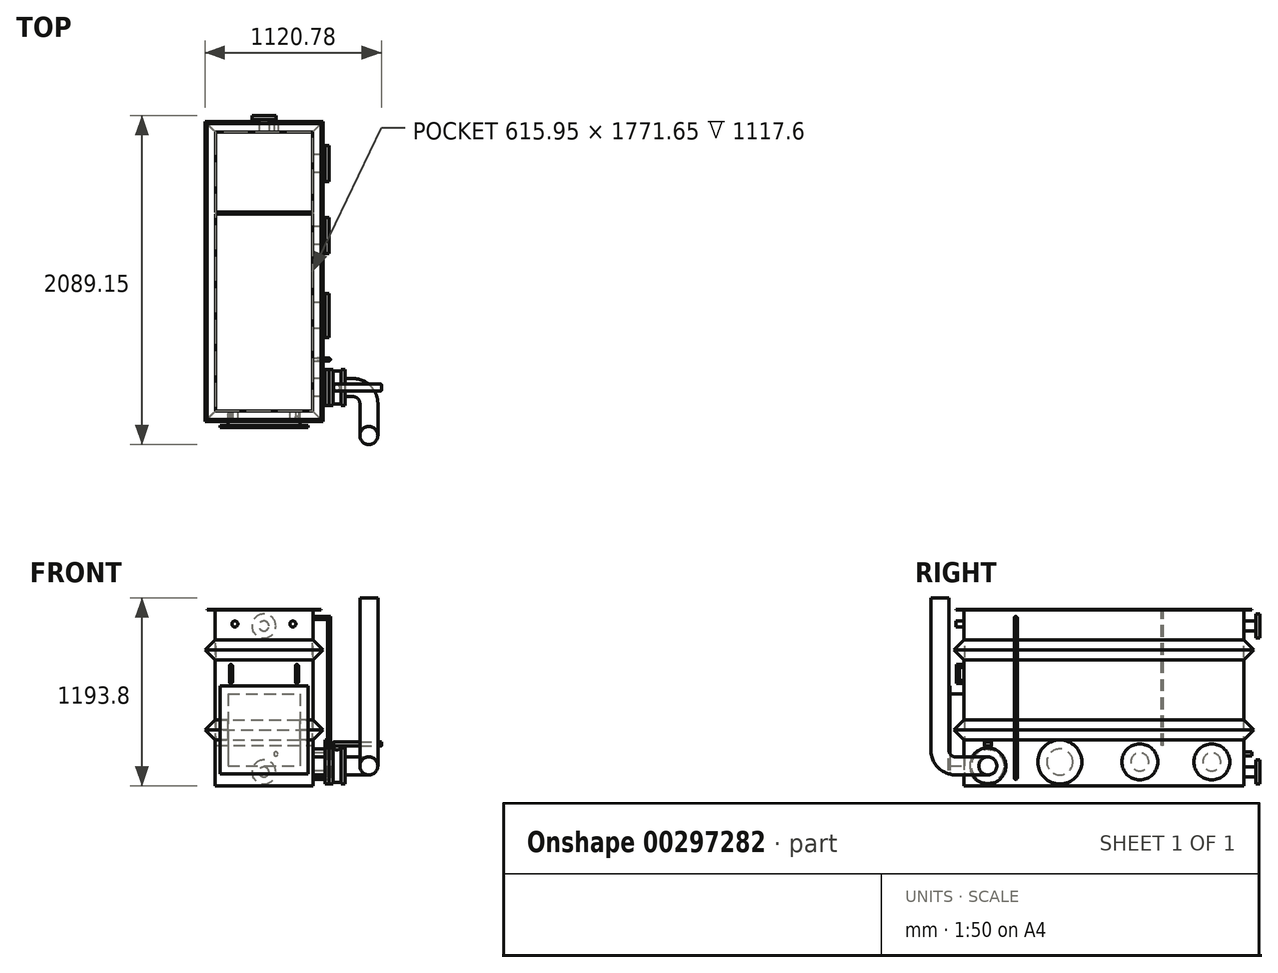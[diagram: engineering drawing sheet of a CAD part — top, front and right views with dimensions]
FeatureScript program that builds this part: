
annotation { "Feature Type Name" : "Feature", "Feature Type Description" : "" }
export const myFeature = defineFeature(function(context is Context, id is Id, definition is map)
    precondition{}
    {
        {
            var Q0;
            Q0=qCreatedBy(makeId("Top.planeOp"),FACE);
            var sketch = newSketch(context, id + "F0", { "sketchPlane" : qUnion([Q0])});
            skLineSegment(sketch, "E0.bottom", {"start": v(-311.15, 889) * mm, "end": v(311.15, 889) * mm});
            skLineSegment(sketch, "E0.top", {"start": v(-311.15, -889) * mm, "end": v(311.15, -889) * mm});
            skLineSegment(sketch, "E0.left", {"start": v(-311.15, 889) * mm, "end": v(-311.15, -889) * mm});
            skLineSegment(sketch, "E0.right", {"start": v(311.15, 889) * mm, "end": v(311.15, -889) * mm});
            skPoint(sketch, "E0.middle", {"position": v(0, 0) * mm});
            skSolve(sketch);
        }
        {
            var Q0;
            Q0 = qSketchRegion(id + "F0", true);
            extrude(context, id + "F1", {"entities" : qUnion([Q0]), "depth" : 558.8 * mm, "hasSecondDirection" : true, "secondDirectionOppositeDirection" : true, "secondDirectionDepth" : 558.8 * mm});
        }
        {
            var Q0;
            Q0=makeQuery(id+"F1.opExtrude","CAP_FACE",FACE,{"disambiguationData":[OSD([sQuery(id+"F0.wireOp",EDGE,"E0.bottom"),sQuery(id+"F0.wireOp",EDGE,"E0.top"),sQuery(id+"F0.wireOp",EDGE,"E0.left"),sQuery(id+"F0.wireOp",EDGE,"E0.right")])],"isStart":false});
            shell(context, id + "F2", {"entities" : qUnion([Q0]), "thickness" : 3.17 * mm});
        }
        {
            var Q0;
            Q0=makeQuery(id+"F1.opExtrude","CAP_FACE",FACE,{"disambiguationData":[OSD([sQuery(id+"F0.wireOp",EDGE,"E0.bottom"),sQuery(id+"F0.wireOp",EDGE,"E0.top"),sQuery(id+"F0.wireOp",EDGE,"E0.left"),sQuery(id+"F0.wireOp",EDGE,"E0.right")])],"isStart":false});
            var sketch = newSketch(context, id + "F3", { "sketchPlane" : qUnion([Q0])});
            skLineSegment(sketch, "E1.bottom", {"start": v(-361.95, 939.8) * mm, "end": v(361.95, 939.8) * mm});
            skLineSegment(sketch, "E1.top", {"start": v(-361.95, -939.8) * mm, "end": v(361.95, -939.8) * mm});
            skLineSegment(sketch, "E1.left", {"start": v(-361.95, 939.8) * mm, "end": v(-361.95, -939.8) * mm});
            skLineSegment(sketch, "E1.right", {"start": v(361.95, 939.8) * mm, "end": v(361.95, -939.8) * mm});
            skLineSegment(sketch, "E2.bottom", {"start": v(-307.97, 885.83) * mm, "end": v(307.97, 885.83) * mm});
            skLineSegment(sketch, "E2.top", {"start": v(-307.97, -885.83) * mm, "end": v(307.97, -885.83) * mm});
            skLineSegment(sketch, "E2.left", {"start": v(-307.97, 885.83) * mm, "end": v(-307.97, -885.83) * mm});
            skLineSegment(sketch, "E2.right", {"start": v(307.97, 885.83) * mm, "end": v(307.97, -885.83) * mm});
            skSolve(sketch);
        }
        {
            var Q0;
            Q0 = qSketchRegion(id + "F3", true);
            extrude(context, id + "F4", {"entities" : qUnion([Q0]), "operationType" : NewBodyOperationType.ADD, "depth" : 3.17 * mm});
        }
        {
            var Q0;
            Q0=makeQuery(id+"F1.opExtrude","SWEPT_FACE",FACE,{"disambiguationData":[OSD([sQuery(id+"F0.wireOp",EDGE,"E0.right")])]});
            var sketch = newSketch(context, id + "F5", { "sketchPlane" : qUnion([Q0])});
            skLineSegment(sketch, "E3", {"start": v(-889, 368.3) * mm, "end": v(-952.5, 304.8) * mm});
            skLineSegment(sketch, "E4", {"start": v(-952.5, 304.8) * mm, "end": v(-889, 241.3) * mm});
            skLineSegment(sketch, "E5", {"start": v(-889, 241.3) * mm, "end": v(-889, 368.3) * mm});
            skLineSegment(sketch, "E6", {"start": v(-889, -139.7) * mm, "end": v(-952.5, -203.2) * mm});
            skLineSegment(sketch, "E7", {"start": v(-952.5, -203.2) * mm, "end": v(-889, -266.7) * mm});
            skLineSegment(sketch, "E8", {"start": v(-889, -266.7) * mm, "end": v(-889, -139.7) * mm});
            skSolve(sketch);
        }
        {
            var Q0;
            Q0 = qSketchRegion(id + "F5", true);
            var Q1;
            Q1=makeQuery(id+"F1.opExtrude","CAP_EDGE",EDGE,{"disambiguationData":[OSD([sQuery(id+"F0.wireOp",EDGE,"E0.top")])],"isStart":true});
            var Q2;
            Q2=makeQuery(id+"F1.opExtrude","CAP_EDGE",EDGE,{"disambiguationData":[OSD([sQuery(id+"F0.wireOp",EDGE,"E0.left")])],"isStart":true});
            var Q3;
            Q3=makeQuery(id+"F1.opExtrude","CAP_EDGE",EDGE,{"disambiguationData":[OSD([sQuery(id+"F0.wireOp",EDGE,"E0.bottom")])],"isStart":true});
            var Q4;
            Q4=makeQuery(id+"F1.opExtrude","CAP_EDGE",EDGE,{"disambiguationData":[OSD([sQuery(id+"F0.wireOp",EDGE,"E0.right")])],"isStart":true});
            sweep(context, id + "F6", {"operationType" : NewBodyOperationType.ADD, "profiles" : qUnion([Q0]), "path" : qUnion([Q1, Q2, Q3, Q4])});
        }
        {
            var Q0;
            {var subQ1=sQuery(id+"F0.wireOp",EDGE,"E0.top");var subQ4=sQuery(id+"F5.wireOp",EDGE,"E4");Q0=makeQuery(id+"F6.boolean.opBoolean","SPLIT",FACE,{"disambiguationData":[TD([makeQuery(id+"F6.opSweep","SWEPT_FACE",FACE,{"disambiguationData":[OSD([subQ1,subQ4])]})])],"derivedFrom":makeQuery(id+"F1.opExtrude","SWEPT_FACE",FACE,{"disambiguationData":[OSD([subQ1])]})});}
            var sketch = newSketch(context, id + "F7", { "sketchPlane" : qUnion([Q0])});
            skLineSegment(sketch, "E9.bottom", {"start": v(-228.6, 25.4) * mm, "end": v(228.6, 25.4) * mm});
            skLineSegment(sketch, "E9.top", {"start": v(-228.6, -431.8) * mm, "end": v(228.6, -431.8) * mm});
            skLineSegment(sketch, "E9.left", {"start": v(-228.6, 25.4) * mm, "end": v(-228.6, -431.8) * mm});
            skLineSegment(sketch, "E9.right", {"start": v(228.6, 25.4) * mm, "end": v(228.6, -431.8) * mm});
            skSolve(sketch);
        }
        {
            var Q0;
            Q0 = qSketchRegion(id + "F7", true);
            extrude(context, id + "F8", {"entities" : qUnion([Q0]), "operationType" : NewBodyOperationType.ADD, "depth" : 88.9 * mm});
        }
        {
            var Q0;
            Q0=makeQuery(id+"F8.opExtrude","CAP_FACE",FACE,{"disambiguationData":[OSD([sQuery(id+"F7.wireOp",EDGE,"E9.bottom"),sQuery(id+"F7.wireOp",EDGE,"E9.top"),sQuery(id+"F7.wireOp",EDGE,"E9.left"),sQuery(id+"F7.wireOp",EDGE,"E9.right")])],"isStart":false});
            var sketch = newSketch(context, id + "F9", { "sketchPlane" : qUnion([Q0])});
            skLineSegment(sketch, "E10.bottom", {"start": v(-279.4, 76.2) * mm, "end": v(279.4, 76.2) * mm});
            skLineSegment(sketch, "E10.top", {"start": v(-279.4, -482.6) * mm, "end": v(279.4, -482.6) * mm});
            skLineSegment(sketch, "E10.left", {"start": v(-279.4, 76.2) * mm, "end": v(-279.4, -482.6) * mm});
            skLineSegment(sketch, "E10.right", {"start": v(279.4, 76.2) * mm, "end": v(279.4, -482.6) * mm});
            skPoint(sketch, "E10.middle", {"position": v(0, -203.2) * mm});
            skSolve(sketch);
        }
        {
            var Q0;
            Q0=makeQuery(id+"F9.imprint","IMPRINT",FACE,{"disambiguationData":[TD([[makeQuery(id+"F9.imprint","IMPRINT",EDGE,{"derivedFrom":sQuery(id+"F9.wireOp",EDGE,"E10.bottom")}),-1.0]])]});
            var Q1;
            Q1=makeQuery(id+"F9.imprint","IMPRINT",FACE,{"disambiguationData":[TD([[makeQuery(id+"F9.imprint","IMPRINT",EDGE,{"derivedFrom":makeQuery(id+"F8.opExtrude","CAP_EDGE",EDGE,{"disambiguationData":[OSD([sQuery(id+"F7.wireOp",EDGE,"E9.bottom")])],"isStart":false})}),-1.0]])]});
            extrude(context, id + "F10", {"entities" : qUnion([Q0, Q1]), "operationType" : NewBodyOperationType.ADD, "depth" : 12.7 * mm});
        }
        {
            var Q0;
            {var subQ0=sQuery(id+"F5.wireOp",EDGE,"E4");var subQ1=sQuery(id+"F0.wireOp",EDGE,"E0.bottom");var subQ3=sQuery(id+"F0.wireOp",EDGE,"E0.right");Q0=makeQuery(id+"F6.boolean.opBoolean","SPLIT",FACE,{"disambiguationData":[TD([makeQuery(id+"F6.opSweep","SWEPT_FACE",FACE,{"disambiguationData":[OSD([subQ1,subQ0])]})])],"derivedFrom":makeQuery(id+"F1.opExtrude","SWEPT_FACE",FACE,{"disambiguationData":[OSD([subQ3])]})});}
            var sketch = newSketch(context, id + "F11", { "sketchPlane" : qUnion([Q0])});
            skCircle(sketch, "E11", {"center": v(-279.4, -406.4) * mm, "radius": 82.55 * mm});
            skCircle(sketch, "E12", {"center": v(228.6, -406.4) * mm, "radius": 57.15 * mm});
            skCircle(sketch, "E13", {"center": v(685.8, -406.4) * mm, "radius": 57.15 * mm});
            skSolve(sketch);
        }
        {
            var Q0;
            Q0 = qSketchRegion(id + "F11", true);
            extrude(context, id + "F12", {"entities" : qUnion([Q0]), "operationType" : NewBodyOperationType.ADD, "depth" : 76.2 * mm});
        }
        {
            var Q0;
            Q0=makeQuery(id+"F12.opExtrude","CAP_FACE",FACE,{"disambiguationData":[OSD([sQuery(id+"F11.wireOp",EDGE,"E13")])],"isStart":false});
            var sketch = newSketch(context, id + "F13", { "sketchPlane" : qUnion([Q0])});
            skCircle(sketch, "E14", {"center": v(-279.4, -406.4) * mm, "radius": 139.7 * mm});
            skCircle(sketch, "E15", {"center": v(228.6, -406.4) * mm, "radius": 114.3 * mm});
            skCircle(sketch, "E16", {"center": v(685.8, -406.4) * mm, "radius": 114.3 * mm});
            skSolve(sketch);
        }
        {
            var Q0;
            Q0 = qSketchRegion(id + "F13", true);
            extrude(context, id + "F14", {"entities" : qUnion([Q0]), "operationType" : NewBodyOperationType.ADD, "depth" : 25.4 * mm});
        }
        {
            var Q0;
            {var subQ0=sQuery(id+"F5.wireOp",EDGE,"E4");var subQ1=sQuery(id+"F0.wireOp",EDGE,"E0.bottom");var subQ3=sQuery(id+"F0.wireOp",EDGE,"E0.right");Q0=makeQuery(id+"F6.boolean.opBoolean","SPLIT",FACE,{"disambiguationData":[TD([makeQuery(id+"F6.opSweep","SWEPT_FACE",FACE,{"disambiguationData":[OSD([subQ1,subQ0])]})])],"derivedFrom":makeQuery(id+"F1.opExtrude","SWEPT_FACE",FACE,{"disambiguationData":[OSD([subQ3])]})});}
            var sketch = newSketch(context, id + "F15", { "sketchPlane" : qUnion([Q0])});
            skCircle(sketch, "E17", {"center": v(-558.8, 508) * mm, "radius": 9.53 * mm});
            skCircle(sketch, "E18", {"center": v(-558.8, -508) * mm, "radius": 9.53 * mm});
            skSolve(sketch);
        }
        {
            var Q0;
            {var subQ0=sQuery(id+"F5.wireOp",EDGE,"E3");var subQ1=sQuery(id+"F0.wireOp",EDGE,"E0.top");Q0=makeQuery(id+"F6.boolean.opBoolean","SPLIT",FACE,{"disambiguationData":[TD([makeQuery(id+"F6.opSweep","SWEPT_FACE",FACE,{"disambiguationData":[OSD([subQ1,subQ0])]})])],"derivedFrom":makeQuery(id+"F1.opExtrude","SWEPT_FACE",FACE,{"disambiguationData":[OSD([subQ1])]})});}
            var sketch = newSketch(context, id + "F16", { "sketchPlane" : qUnion([Q0])});
            skLineSegment(sketch, "E19", {"start": v(311.15, 508) * mm, "end": v(412.75, 508) * mm});
            skLineSegment(sketch, "E20", {"start": v(412.75, 508) * mm, "end": v(412.75, -508) * mm});
            skLineSegment(sketch, "E21", {"start": v(412.75, -508) * mm, "end": v(311.15, -508) * mm});
            skSolve(sketch);
        }
        {
            var Q0;
            Q0=makeQuery(id+"F15.imprint","IMPRINT",FACE,{"disambiguationData":[TD([[makeQuery(id+"F15.imprint","IMPRINT",EDGE,{"derivedFrom":sQuery(id+"F15.wireOp",EDGE,"E17")}),1.0]])]});
            var Q1;
            Q1=sQuery(id+"F16.wireOp",EDGE,"E19");
            var Q2;
            Q2=sQuery(id+"F16.wireOp",EDGE,"E20");
            var Q3;
            Q3=sQuery(id+"F16.wireOp",EDGE,"E21");
            sweep(context, id + "F17", {"operationType" : NewBodyOperationType.ADD, "profiles" : qUnion([Q0]), "path" : qUnion([Q1, Q2, Q3])});
        }
        {
            var Q0;
            Q0=makeQuery(id+"F4.opExtrude","CAP_FACE",FACE,{"disambiguationData":[OSD([sQuery(id+"F3.wireOp",EDGE,"E1.bottom"),sQuery(id+"F3.wireOp",EDGE,"E1.top"),sQuery(id+"F3.wireOp",EDGE,"E1.left"),sQuery(id+"F3.wireOp",EDGE,"E1.right"),sQuery(id+"F3.wireOp",EDGE,"E2.bottom"),sQuery(id+"F3.wireOp",EDGE,"E2.top"),sQuery(id+"F3.wireOp",EDGE,"E2.left"),sQuery(id+"F3.wireOp",EDGE,"E2.right")])],"isStart":false});
            var sketch = newSketch(context, id + "F18", { "sketchPlane" : qUnion([Q0])});
            skLineSegment(sketch, "E22.bottom", {"start": v(-307.98, 377.83) * mm, "end": v(307.98, 377.83) * mm});
            skLineSegment(sketch, "E22.top", {"start": v(-307.98, 365.13) * mm, "end": v(307.98, 365.13) * mm});
            skLineSegment(sketch, "E22.left", {"start": v(-307.98, 377.83) * mm, "end": v(-307.98, 365.13) * mm});
            skLineSegment(sketch, "E22.right", {"start": v(307.98, 377.83) * mm, "end": v(307.98, 365.13) * mm});
            skSolve(sketch);
        }
        {
            var Q0;
            Q0 = qSketchRegion(id + "F18", true);
            extrude(context, id + "F19", {"entities" : qUnion([Q0]), "operationType" : NewBodyOperationType.ADD, "oppositeDirection" : true, "depth" : 863.6 * mm});
        }
        {
            var Q0;
            {var subQ0=sQuery(id+"F5.wireOp",EDGE,"E4");var subQ1=sQuery(id+"F0.wireOp",EDGE,"E0.bottom");Q0=makeQuery(id+"F6.boolean.opBoolean","SPLIT",FACE,{"disambiguationData":[TD([makeQuery(id+"F6.opSweep","SWEPT_FACE",FACE,{"disambiguationData":[OSD([subQ1,subQ0])]})])],"derivedFrom":makeQuery(id+"F1.opExtrude","SWEPT_FACE",FACE,{"disambiguationData":[OSD([subQ1])]})});}
            var sketch = newSketch(context, id + "F20", { "sketchPlane" : qUnion([Q0])});
            skCircle(sketch, "E23", {"center": v(0, 457.2) * mm, "radius": 31.75 * mm});
            skCircle(sketch, "E24", {"center": v(0, -469.9) * mm, "radius": 31.75 * mm});
            skSolve(sketch);
        }
        {
            var Q0;
            Q0 = qSketchRegion(id + "F20", true);
            extrude(context, id + "F21", {"entities" : qUnion([Q0]), "operationType" : NewBodyOperationType.ADD, "depth" : 76.2 * mm});
        }
        {
            var Q0;
            {var subQ2=sQuery(id+"F5.wireOp",EDGE,"E7");var subQ3=sQuery(id+"F0.wireOp",EDGE,"E0.bottom");Q0=makeQuery(id+"F6.boolean.opBoolean","SPLIT",FACE,{"disambiguationData":[TD([makeQuery(id+"F6.opSweep","SWEPT_FACE",FACE,{"disambiguationData":[OSD([subQ3,subQ2])]})])],"derivedFrom":makeQuery(id+"F1.opExtrude","SWEPT_FACE",FACE,{"disambiguationData":[OSD([subQ3])]})});}
            var sketch = newSketch(context, id + "F22", { "sketchPlane" : qUnion([Q0])});
            skCircle(sketch, "E25", {"center": v(-76.2, -355.6) * mm, "radius": 12.7 * mm});
            skSolve(sketch);
        }
        {
            var Q0;
            Q0 = qSketchRegion(id + "F22", true);
            extrude(context, id + "F23", {"entities" : qUnion([Q0]), "operationType" : NewBodyOperationType.ADD, "depth" : 50.8 * mm});
        }
        {
            var Q0;
            {var subQ1=sQuery(id+"F5.wireOp",EDGE,"E7");var subQ2=sQuery(id+"F0.wireOp",EDGE,"E0.bottom");var subQ3=sQuery(id+"F0.wireOp",EDGE,"E0.right");Q0=makeQuery(id+"F6.boolean.opBoolean","SPLIT",FACE,{"disambiguationData":[TD([makeQuery(id+"F6.opSweep","SWEPT_FACE",FACE,{"disambiguationData":[OSD([subQ2,subQ1])]})])],"derivedFrom":makeQuery(id+"F1.opExtrude","SWEPT_FACE",FACE,{"disambiguationData":[OSD([subQ3])]})});}
            var sketch = newSketch(context, id + "F24", { "sketchPlane" : qUnion([Q0])});
            skCircle(sketch, "E26", {"center": v(-736.6, -431.8) * mm, "radius": 57.15 * mm});
            skSolve(sketch);
        }
        {
            var Q0;
            Q0=makeQuery(id+"F24.imprint","IMPRINT",FACE,{"disambiguationData":[TD([[makeQuery(id+"F24.imprint","IMPRINT",EDGE,{"derivedFrom":sQuery(id+"F24.wireOp",EDGE,"E26")}),1.0]])]});
            extrude(context, id + "F25", {"entities" : qUnion([Q0]), "operationType" : NewBodyOperationType.ADD, "depth" : 76.2 * mm});
        }
        {
            var Q0;
            Q0=makeQuery(id+"F25.opExtrude","CAP_FACE",FACE,{"disambiguationData":[OSD([sQuery(id+"F24.wireOp",EDGE,"E26")])],"isStart":false});
            var sketch = newSketch(context, id + "F26", { "sketchPlane" : qUnion([Q0])});
            skCircle(sketch, "E27", {"center": v(-736.6, -431.8) * mm, "radius": 114.3 * mm});
            skSolve(sketch);
        }
        {
            var Q0;
            Q0 = qSketchRegion(id + "F26", true);
            extrude(context, id + "F27", {"entities" : qUnion([Q0]), "operationType" : NewBodyOperationType.ADD, "depth" : 25.4 * mm});
        }
        {
            var Q0;
            Q0=makeQuery(id+"F27.opExtrude","CAP_FACE",FACE,{"disambiguationData":[OSD([sQuery(id+"F26.wireOp",EDGE,"E27")])],"isStart":false});
            var sketch = newSketch(context, id + "F28", { "sketchPlane" : qUnion([Q0])});
            skCircle(sketch, "E28", {"center": v(-736.6, -431.8) * mm, "radius": 114.3 * mm});
            skSolve(sketch);
        }
        {
            var Q0;
            Q0=makeQuery(id+"F28.imprint","IMPRINT",FACE,{"disambiguationData":[TD([[makeQuery(id+"F28.imprint","IMPRINT",EDGE,{"derivedFrom":sQuery(id+"F28.wireOp",EDGE,"E28")}),1.0]])]});
            extrude(context, id + "F29", {"entities" : qUnion([Q0]), "depth" : 25.4 * mm});
        }
        {
            var Q0;
            Q0=makeQuery(id+"F29.opExtrude","CAP_FACE",FACE,{"disambiguationData":[OSD([sQuery(id+"F28.wireOp",EDGE,"E28")])],"isStart":false});
            var sketch = newSketch(context, id + "F30", { "sketchPlane" : qUnion([Q0])});
            skCircle(sketch, "E29", {"center": v(-736.6, -431.8) * mm, "radius": 104.78 * mm});
            skSolve(sketch);
        }
        {
            var Q0;
            Q0 = qSketchRegion(id + "F30", true);
            extrude(context, id + "F31", {"entities" : qUnion([Q0]), "depth" : 50.8 * mm});
        }
        {
            var Q0;
            Q0=makeQuery(id+"F31.opExtrude","CAP_FACE",FACE,{"disambiguationData":[OSD([sQuery(id+"F30.wireOp",EDGE,"E29")])],"isStart":false});
            var sketch = newSketch(context, id + "F32", { "sketchPlane" : qUnion([Q0])});
            skCircle(sketch, "E30", {"center": v(-736.6, -431.8) * mm, "radius": 114.3 * mm});
            skSolve(sketch);
        }
        {
            var Q0;
            Q0 = qSketchRegion(id + "F32", true);
            extrude(context, id + "F33", {"entities" : qUnion([Q0]), "depth" : 25.4 * mm});
        }
        {
            var Q0;
            Q0=makeQuery(id+"F33.opExtrude","CAP_FACE",FACE,{"disambiguationData":[OSD([sQuery(id+"F32.wireOp",EDGE,"E30")])],"isStart":false});
            var sketch = newSketch(context, id + "F34", { "sketchPlane" : qUnion([Q0])});
            skCircle(sketch, "E31", {"center": v(-736.6, -431.8) * mm, "radius": 57.15 * mm});
            skSolve(sketch);
        }
        {
            var Q0;
            Q0=makeQuery(id+"F1.opExtrude","CAP_FACE",FACE,{"disambiguationData":[OSD([sQuery(id+"F0.wireOp",EDGE,"E0.bottom"),sQuery(id+"F0.wireOp",EDGE,"E0.top"),sQuery(id+"F0.wireOp",EDGE,"E0.left"),sQuery(id+"F0.wireOp",EDGE,"E0.right")])],"isStart":true});
            var sketch = newSketch(context, id + "F35", { "sketchPlane" : qUnion([Q0])});
            skLineSegment(sketch, "E32", {"start": v(514.35, 736.6) * mm, "end": v(565.15, 736.6) * mm});
            skLineSegment(sketch, "E33", {"start": v(666.75, 838.2) * mm, "end": v(666.75, 889) * mm});
            skPoint(sketch, "E34.visualSharp", {"position": v(666.75, 736.6) * mm});
            skArc(sketch, "E34.filletArc", {"start": v(565.15, 736.6) * mm, "mid": v(637, 766.36) * mm, "end": v(666.75, 838.2) * mm});
            skSolve(sketch);
        }
        {
            var Q0;
            Q0=makeQuery(id+"F34.imprint","IMPRINT",FACE,{"disambiguationData":[TD([[makeQuery(id+"F34.imprint","IMPRINT",EDGE,{"derivedFrom":sQuery(id+"F34.wireOp",EDGE,"E31")}),1.0]])]});
            var Q1;
            Q1=sQuery(id+"F35.wireOp",EDGE,"E32");
            var Q2;
            Q2=sQuery(id+"F35.wireOp",EDGE,"E34.filletArc");
            var Q3;
            Q3=sQuery(id+"F35.wireOp",EDGE,"E33");
            sweep(context, id + "F36", {"operationType" : NewBodyOperationType.ADD, "profiles" : qUnion([Q0]), "path" : qUnion([Q1, Q2, Q3])});
        }
        {
            var Q0;
            {var subQ1=sQuery(id+"F5.wireOp",EDGE,"E7");var subQ2=sQuery(id+"F0.wireOp",EDGE,"E0.bottom");var subQ3=sQuery(id+"F0.wireOp",EDGE,"E0.right");Q0=makeQuery(id+"F6.boolean.opBoolean","SPLIT",FACE,{"disambiguationData":[TD([makeQuery(id+"F6.opSweep","SWEPT_FACE",FACE,{"disambiguationData":[OSD([subQ2,subQ1])]})])],"derivedFrom":makeQuery(id+"F1.opExtrude","SWEPT_FACE",FACE,{"disambiguationData":[OSD([subQ3])]})});}
            var sketch = newSketch(context, id + "F37", { "sketchPlane" : qUnion([Q0])});
            skLineSegment(sketch, "E35", {"start": v(-889, -431.8) * mm, "end": v(-939.8, -431.8) * mm});
            skLineSegment(sketch, "E36", {"start": v(-1041.4, -330.2) * mm, "end": v(-1041.4, 635) * mm});
            skPoint(sketch, "E37.visualSharp", {"position": v(-1041.4, -431.8) * mm});
            skArc(sketch, "E37.filletArc", {"start": v(-1041.4, -330.2) * mm, "mid": v(-1011.64, -402.04) * mm, "end": v(-939.8, -431.8) * mm});
            skPoint(sketch, "E38", {"position": v(-736.6, -431.8) * mm});
            skSolve(sketch);
        }
        {
            var Q0;
            Q0=makeQuery(id+"F36.opSweep","CAP_FACE",FACE,{"disambiguationData":[OSD([sQuery(id+"F34.wireOp",EDGE,"E31"),sQuery(id+"F35.wireOp",VERTEX,"E33.end")])],"isStart":false});
            var Q1;
            Q1=sQuery(id+"F37.wireOp",EDGE,"E35");
            var Q2;
            Q2=sQuery(id+"F37.wireOp",EDGE,"E37.filletArc");
            var Q3;
            Q3=sQuery(id+"F37.wireOp",EDGE,"E36");
            sweep(context, id + "F38", {"operationType" : NewBodyOperationType.ADD, "profiles" : qUnion([Q0]), "path" : qUnion([Q1, Q2, Q3])});
        }
        {
            var Q0;
            Q0=sQuery(id+"F24.wireOp",VERTEX,"E26.center");
            var Q1;
            Q1=makeQuery(id+"F1.opExtrude","CAP_FACE",FACE,{"disambiguationData":[OSD([sQuery(id+"F0.wireOp",EDGE,"E0.bottom"),sQuery(id+"F0.wireOp",EDGE,"E0.top"),sQuery(id+"F0.wireOp",EDGE,"E0.left"),sQuery(id+"F0.wireOp",EDGE,"E0.right")])],"isStart":true});
            cPlane(context, id + "F39", {"entities" : qUnion([Q0, Q1]), "cplaneType" : CPlaneType.PLANE_POINT, "offset" : 25.4 * mm, "width" : 152.4 * mm, "height" : 152.4 * mm});
        }
        {
            var Q0;
            Q0=qCreatedBy(id+"F39.planeOp",FACE);
            var sketch = newSketch(context, id + "F40", { "sketchPlane" : qUnion([Q0])});
            skCircle(sketch, "E39", {"center": v(463.55, 736.6) * mm, "radius": 19.05 * mm});
            skSolve(sketch);
        }
        {
            var Q0;
            Q0 = qSketchRegion(id + "F40", true);
            extrude(context, id + "F41", {"entities" : qUnion([Q0]), "operationType" : NewBodyOperationType.ADD, "oppositeDirection" : true, "depth" : 127 * mm});
        }
        {
            var Q0;
            Q0=makeQuery(id+"F41.opExtrude","CAP_FACE",FACE,{"disambiguationData":[OSD([sQuery(id+"F40.wireOp",EDGE,"E39")])],"isStart":false});
            var sketch = newSketch(context, id + "F42", { "sketchPlane" : qUnion([Q0])});
            skLineSegment(sketch, "E40.bottom", {"start": v(446.4, -714.38) * mm, "end": v(741.04, -714.38) * mm});
            skLineSegment(sketch, "E40.top", {"start": v(446.4, -758.83) * mm, "end": v(741.04, -758.83) * mm});
            skLineSegment(sketch, "E40.left", {"start": v(441.32, -719.45) * mm, "end": v(441.32, -753.75) * mm});
            skLineSegment(sketch, "E40.right", {"start": v(746.12, -719.45) * mm, "end": v(746.12, -753.75) * mm});
            skPoint(sketch, "E41.visualSharp", {"position": v(441.32, -714.38) * mm});
            skArc(sketch, "E41.filletArc", {"start": v(446.4, -714.38) * mm, "mid": v(442.81, -715.86) * mm, "end": v(441.32, -719.45) * mm});
            skPoint(sketch, "E42.visualSharp", {"position": v(441.32, -758.83) * mm});
            skArc(sketch, "E42.filletArc", {"start": v(441.32, -753.75) * mm, "mid": v(442.81, -757.34) * mm, "end": v(446.4, -758.82) * mm});
            skPoint(sketch, "E43.visualSharp", {"position": v(746.12, -714.38) * mm});
            skArc(sketch, "E43.filletArc", {"start": v(746.12, -719.45) * mm, "mid": v(744.64, -715.86) * mm, "end": v(741.04, -714.38) * mm});
            skPoint(sketch, "E44.visualSharp", {"position": v(746.12, -758.83) * mm});
            skArc(sketch, "E44.filletArc", {"start": v(741.04, -758.82) * mm, "mid": v(744.64, -757.34) * mm, "end": v(746.12, -753.75) * mm});
            skSolve(sketch);
        }
        {
            var Q0;
            Q0 = qSketchRegion(id + "F42", true);
            extrude(context, id + "F43", {"entities" : qUnion([Q0]), "operationType" : NewBodyOperationType.ADD, "depth" : 25.4 * mm});
        }
        {
            var Q0;
            Q0=makeQuery(id+"F21.opExtrude","CAP_FACE",FACE,{"disambiguationData":[OSD([sQuery(id+"F20.wireOp",EDGE,"E23")])],"isStart":false});
            var sketch = newSketch(context, id + "F44", { "sketchPlane" : qUnion([Q0])});
            skCircle(sketch, "E45", {"center": v(0, 457.2) * mm, "radius": 76.2 * mm});
            skCircle(sketch, "E46", {"center": v(0, -469.9) * mm, "radius": 76.2 * mm});
            skSolve(sketch);
        }
        {
            var Q0;
            Q0 = qSketchRegion(id + "F44", true);
            extrude(context, id + "F45", {"entities" : qUnion([Q0]), "operationType" : NewBodyOperationType.ADD, "depth" : 25.4 * mm});
        }
        {
            var Q0;
            {var subQ0=sQuery(id+"F5.wireOp",EDGE,"E7");var subQ1=sQuery(id+"F0.wireOp",EDGE,"E0.top");Q0=makeQuery(id+"F6.boolean.opBoolean","SPLIT",FACE,{"disambiguationData":[TD([makeQuery(id+"F6.opSweep","SWEPT_FACE",FACE,{"disambiguationData":[OSD([subQ1,subQ0])]})])],"derivedFrom":makeQuery(id+"F1.opExtrude","SWEPT_FACE",FACE,{"disambiguationData":[OSD([subQ1])]})});}
            var sketch = newSketch(context, id + "F46", { "sketchPlane" : qUnion([Q0])});
            skCircle(sketch, "E47", {"center": v(-184.15, 469.9) * mm, "radius": 19.05 * mm});
            skCircle(sketch, "E48", {"center": v(184.15, 469.9) * mm, "radius": 19.05 * mm});
            skSolve(sketch);
        }
        {
            var Q0;
            Q0=makeQuery(id+"F46.imprint","IMPRINT",FACE,{"disambiguationData":[TD([[makeQuery(id+"F46.imprint","IMPRINT",EDGE,{"derivedFrom":sQuery(id+"F46.wireOp",EDGE,"E47")}),1.0]])]});
            var Q1;
            Q1=makeQuery(id+"F46.imprint","IMPRINT",FACE,{"disambiguationData":[TD([[makeQuery(id+"F46.imprint","IMPRINT",EDGE,{"derivedFrom":sQuery(id+"F46.wireOp",EDGE,"E48")}),1.0]])]});
            extrude(context, id + "F47", {"entities" : qUnion([Q0, Q1]), "operationType" : NewBodyOperationType.ADD, "depth" : 50.8 * mm});
        }
        {
            var Q0;
            {var subQ1=sQuery(id+"F0.wireOp",EDGE,"E0.top");var subQ2=sQuery(id+"F5.wireOp",EDGE,"E4");Q0=makeQuery(id+"F6.boolean.opBoolean","SPLIT",FACE,{"disambiguationData":[TD([makeQuery(id+"F6.opSweep","SWEPT_FACE",FACE,{"disambiguationData":[OSD([subQ1,subQ2])]})])],"derivedFrom":makeQuery(id+"F1.opExtrude","SWEPT_FACE",FACE,{"disambiguationData":[OSD([subQ1])]})});}
            var sketch = newSketch(context, id + "F48", { "sketchPlane" : qUnion([Q0])});
            skCircle(sketch, "E49", {"center": v(-209.55, 203.2) * mm, "radius": 9.53 * mm});
            skCircle(sketch, "E50", {"center": v(209.55, 203.2) * mm, "radius": 9.53 * mm});
            skSolve(sketch);
        }
        {
            var Q0;
            {var subQ1=sQuery(id+"F0.wireOp",EDGE,"E0.bottom");var subQ2=sQuery(id+"F5.wireOp",EDGE,"E4");var subQ4=sQuery(id+"F0.wireOp",EDGE,"E0.right");Q0=makeQuery(id+"F6.boolean.opBoolean","SPLIT",FACE,{"disambiguationData":[TD([makeQuery(id+"F6.opSweep","SWEPT_FACE",FACE,{"disambiguationData":[OSD([subQ1,subQ2])]})])],"derivedFrom":makeQuery(id+"F1.opExtrude","SWEPT_FACE",FACE,{"disambiguationData":[OSD([subQ4])]})});}
            var sketch = newSketch(context, id + "F49", { "sketchPlane" : qUnion([Q0])});
            skLineSegment(sketch, "E51", {"start": v(-889, 215.9) * mm, "end": v(-939.8, 215.9) * mm});
            skLineSegment(sketch, "E52", {"start": v(-939.8, 215.9) * mm, "end": v(-939.8, 88.9) * mm});
            skLineSegment(sketch, "E53", {"start": v(-939.8, 88.9) * mm, "end": v(-889, 88.9) * mm});
            skSolve(sketch);
        }
        {
            var Q0;
            Q0=makeQuery(id+"F48.imprint","IMPRINT",FACE,{"disambiguationData":[TD([[makeQuery(id+"F48.imprint","IMPRINT",EDGE,{"derivedFrom":sQuery(id+"F48.wireOp",EDGE,"E49")}),1.0]])]});
            var Q1;
            Q1=makeQuery(id+"F48.imprint","IMPRINT",FACE,{"disambiguationData":[TD([[makeQuery(id+"F48.imprint","IMPRINT",EDGE,{"derivedFrom":sQuery(id+"F48.wireOp",EDGE,"E50")}),1.0]])]});
            var Q2;
            Q2=sQuery(id+"F49.wireOp",EDGE,"E51");
            var Q3;
            Q3=sQuery(id+"F49.wireOp",EDGE,"E52");
            var Q4;
            Q4=sQuery(id+"F49.wireOp",EDGE,"E53");
            sweep(context, id + "F50", {"operationType" : NewBodyOperationType.ADD, "profiles" : qUnion([Q0, Q1]), "path" : qUnion([Q2, Q3, Q4])});
        }
    });
